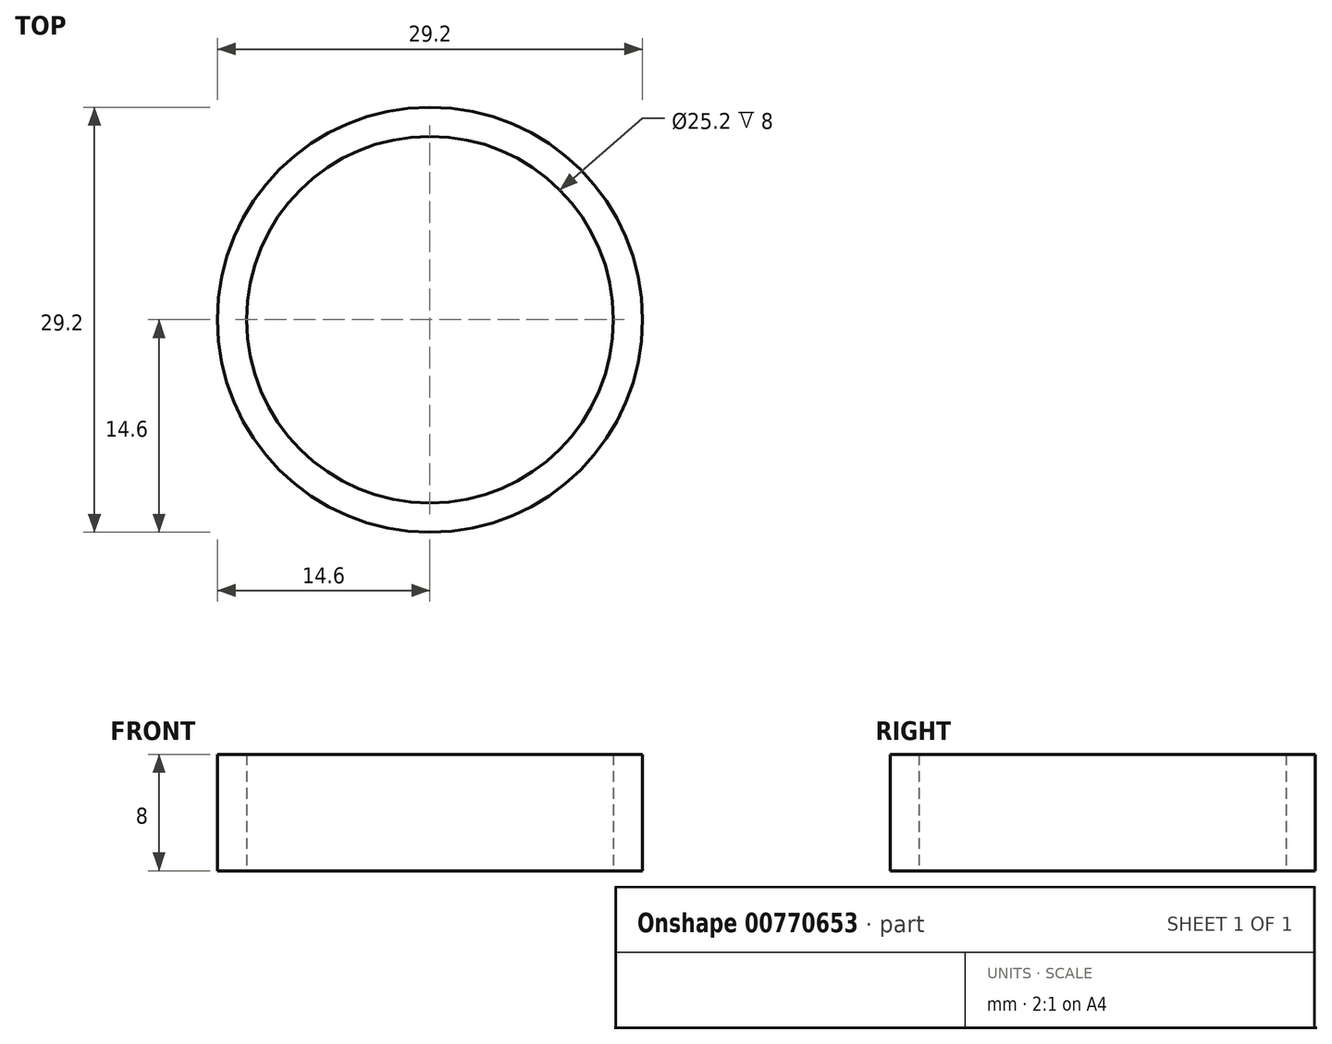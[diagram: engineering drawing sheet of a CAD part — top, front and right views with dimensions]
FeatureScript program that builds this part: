
annotation { "Feature Type Name" : "Feature", "Feature Type Description" : "" }
export const myFeature = defineFeature(function(context is Context, id is Id, definition is map)
    precondition{}
    {
        {
            var Q0;
            Q0=qCreatedBy(makeId("Top.planeOp"),FACE);
            var sketch = newSketch(context, id + "F0", { "sketchPlane" : qUnion([Q0])});
            skCircle(sketch, "E0", {"center": v(0, 0) * mm, "radius": 12.6 * mm});
            skCircle(sketch, "E1", {"center": v(0, 0) * mm, "radius": 14.6 * mm});
            skLineSegment(sketch, "E2", {"start": v(-12.6, 0) * mm, "end": v(-14.6, 0) * mm, "construction": true});
            skSolve(sketch);
        }
        {
            var Q0;
            Q0=makeQuery(id+"F0.imprint","IMPRINT",FACE,{"disambiguationData":[TD([[makeQuery(id+"F0.imprint","IMPRINT",EDGE,{"derivedFrom":sQuery(id+"F0.wireOp",EDGE,"E0")}),-1.0]])]});
            extrude(context, id + "F1", {"entities" : qUnion([Q0]), "depth" : 8 * mm, "offsetDistance" : 25 * mm});
        }
    });
